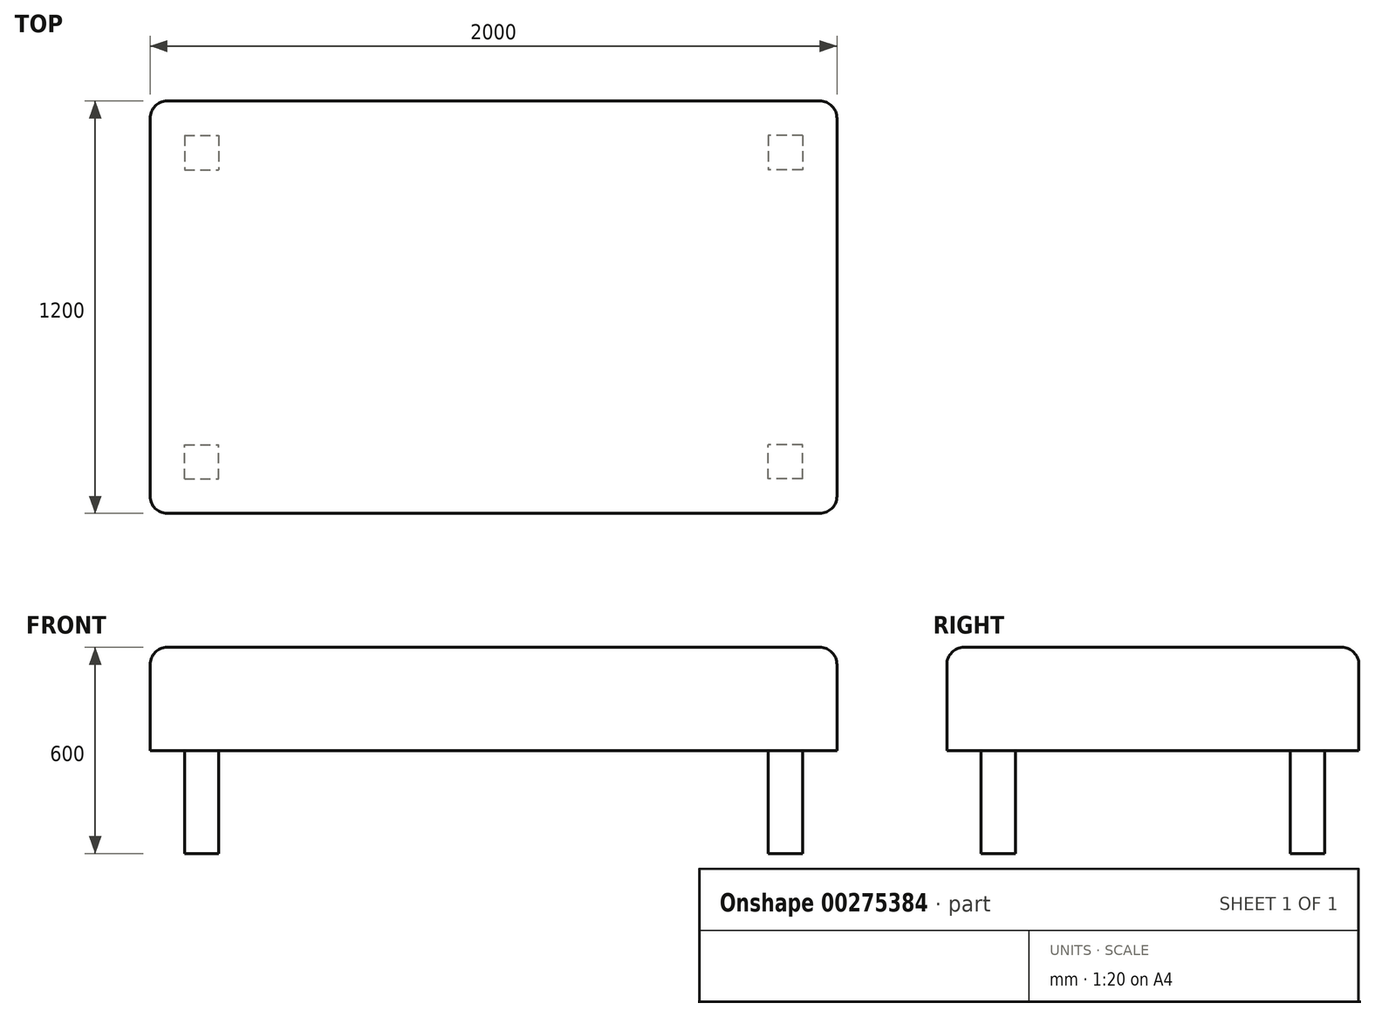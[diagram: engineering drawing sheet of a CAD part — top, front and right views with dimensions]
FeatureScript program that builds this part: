
annotation { "Feature Type Name" : "Feature", "Feature Type Description" : "" }
export const myFeature = defineFeature(function(context is Context, id is Id, definition is map)
    precondition{}
    {
        {
            var Q0;
            Q0=qCreatedBy(makeId("Top.planeOp"),FACE);
            var sketch = newSketch(context, id + "F0", { "sketchPlane" : qUnion([Q0])});
            skLineSegment(sketch, "E0.bottom", {"start": v(1000, 600) * mm, "end": v(-1000, 600) * mm});
            skLineSegment(sketch, "E0.top", {"start": v(1000, -600) * mm, "end": v(-1000, -600) * mm});
            skLineSegment(sketch, "E0.left", {"start": v(1000, 600) * mm, "end": v(1000, -600) * mm});
            skLineSegment(sketch, "E0.right", {"start": v(-1000, 600) * mm, "end": v(-1000, -600) * mm});
            skPoint(sketch, "E0.middle", {"position": v(0, 0) * mm});
            skSolve(sketch);
        }
        {
            var Q0;
            Q0 = qSketchRegion(id + "F0", true);
            extrude(context, id + "F1", {"entities" : qUnion([Q0]), "depth" : 300 * mm});
        }
        {
            var Q0;
            Q0=makeQuery(id+"F1.opExtrude","CAP_FACE",FACE,{"disambiguationData":[OSD([sQuery(id+"F0.wireOp",EDGE,"E0.bottom"),sQuery(id+"F0.wireOp",EDGE,"E0.top"),sQuery(id+"F0.wireOp",EDGE,"E0.left"),sQuery(id+"F0.wireOp",EDGE,"E0.right")])],"isStart":false});
            var Q1;
            Q1=makeQuery(id+"F1.opExtrude","SWEPT_EDGE",EDGE,{"disambiguationData":[OSD([sQuery(id+"F0.wireOp",EDGE,"E0.top"),sQuery(id+"F0.wireOp",EDGE,"E0.right")])]});
            var Q2;
            Q2=makeQuery(id+"F1.opExtrude","SWEPT_EDGE",EDGE,{"disambiguationData":[OSD([sQuery(id+"F0.wireOp",EDGE,"E0.top"),sQuery(id+"F0.wireOp",EDGE,"E0.left")])]});
            var Q3;
            Q3=makeQuery(id+"F1.opExtrude","SWEPT_EDGE",EDGE,{"disambiguationData":[OSD([sQuery(id+"F0.wireOp",EDGE,"E0.bottom"),sQuery(id+"F0.wireOp",EDGE,"E0.left")])]});
            var Q4;
            Q4=makeQuery(id+"F1.opExtrude","SWEPT_EDGE",EDGE,{"disambiguationData":[OSD([sQuery(id+"F0.wireOp",EDGE,"E0.bottom"),sQuery(id+"F0.wireOp",EDGE,"E0.right")])]});
            fillet(context, id + "F2", {"entities" : qUnion([Q0, Q1, Q2, Q3, Q4]), "radius" : 50 * mm, "tangentPropagation" : true, "allowEdgeOverflow" : false});
        }
        {
            var Q0;
            Q0=makeQuery(id+"F1.opExtrude","CAP_FACE",FACE,{"disambiguationData":[OSD([sQuery(id+"F0.wireOp",EDGE,"E0.bottom"),sQuery(id+"F0.wireOp",EDGE,"E0.top"),sQuery(id+"F0.wireOp",EDGE,"E0.left"),sQuery(id+"F0.wireOp",EDGE,"E0.right")])],"isStart":true});
            var sketch = newSketch(context, id + "F3", { "sketchPlane" : qUnion([Q0])});
            skLineSegment(sketch, "E1.bottom", {"start": v(-900, 500) * mm, "end": v(-800, 500) * mm});
            skLineSegment(sketch, "E1.top", {"start": v(-900, 400) * mm, "end": v(-800, 400) * mm});
            skLineSegment(sketch, "E1.left", {"start": v(-900, 500) * mm, "end": v(-900, 400) * mm});
            skLineSegment(sketch, "E1.right", {"start": v(-800, 500) * mm, "end": v(-800, 400) * mm});
            skLineSegment(sketch, "E2", {"start": v(-1552.23, 0) * mm, "end": v(1382.63, 0) * mm, "construction": true});
            skLineSegment(sketch, "E3", {"start": v(0, 891.9) * mm, "end": v(0, -789.68) * mm, "construction": true});
            skLineSegment(sketch, "E4.MirrorCS", {"start": v(900, 500) * mm, "end": v(800, 500) * mm});
            skLineSegment(sketch, "E5.MirrorCS", {"start": v(800, 500) * mm, "end": v(800, 400) * mm});
            skLineSegment(sketch, "E6.MirrorCS", {"start": v(900, 400) * mm, "end": v(800, 400) * mm});
            skLineSegment(sketch, "E7.MirrorCS", {"start": v(900, 500) * mm, "end": v(900, 400) * mm});
            skLineSegment(sketch, "E8.MirrorCS", {"start": v(-900, -500) * mm, "end": v(-800, -500) * mm});
            skLineSegment(sketch, "E9.MirrorCS", {"start": v(-900, -400) * mm, "end": v(-800, -400) * mm});
            skLineSegment(sketch, "E10.MirrorCS", {"start": v(-900, -500) * mm, "end": v(-900, -400) * mm});
            skLineSegment(sketch, "E11.MirrorCS", {"start": v(-800, -500) * mm, "end": v(-800, -400) * mm});
            skLineSegment(sketch, "E12.MirrorCS", {"start": v(900, -500) * mm, "end": v(900, -400) * mm});
            skLineSegment(sketch, "E13.MirrorCS", {"start": v(900, -400) * mm, "end": v(800, -400) * mm});
            skLineSegment(sketch, "E14.MirrorCS", {"start": v(800, -500) * mm, "end": v(800, -400) * mm});
            skLineSegment(sketch, "E15.MirrorCS", {"start": v(900, -500) * mm, "end": v(800, -500) * mm});
            skSolve(sketch);
        }
        {
            var Q0;
            Q0 = qSketchRegion(id + "F3", true);
            extrude(context, id + "F4", {"entities" : qUnion([Q0]), "operationType" : NewBodyOperationType.ADD, "depth" : 300 * mm});
        }
    });
